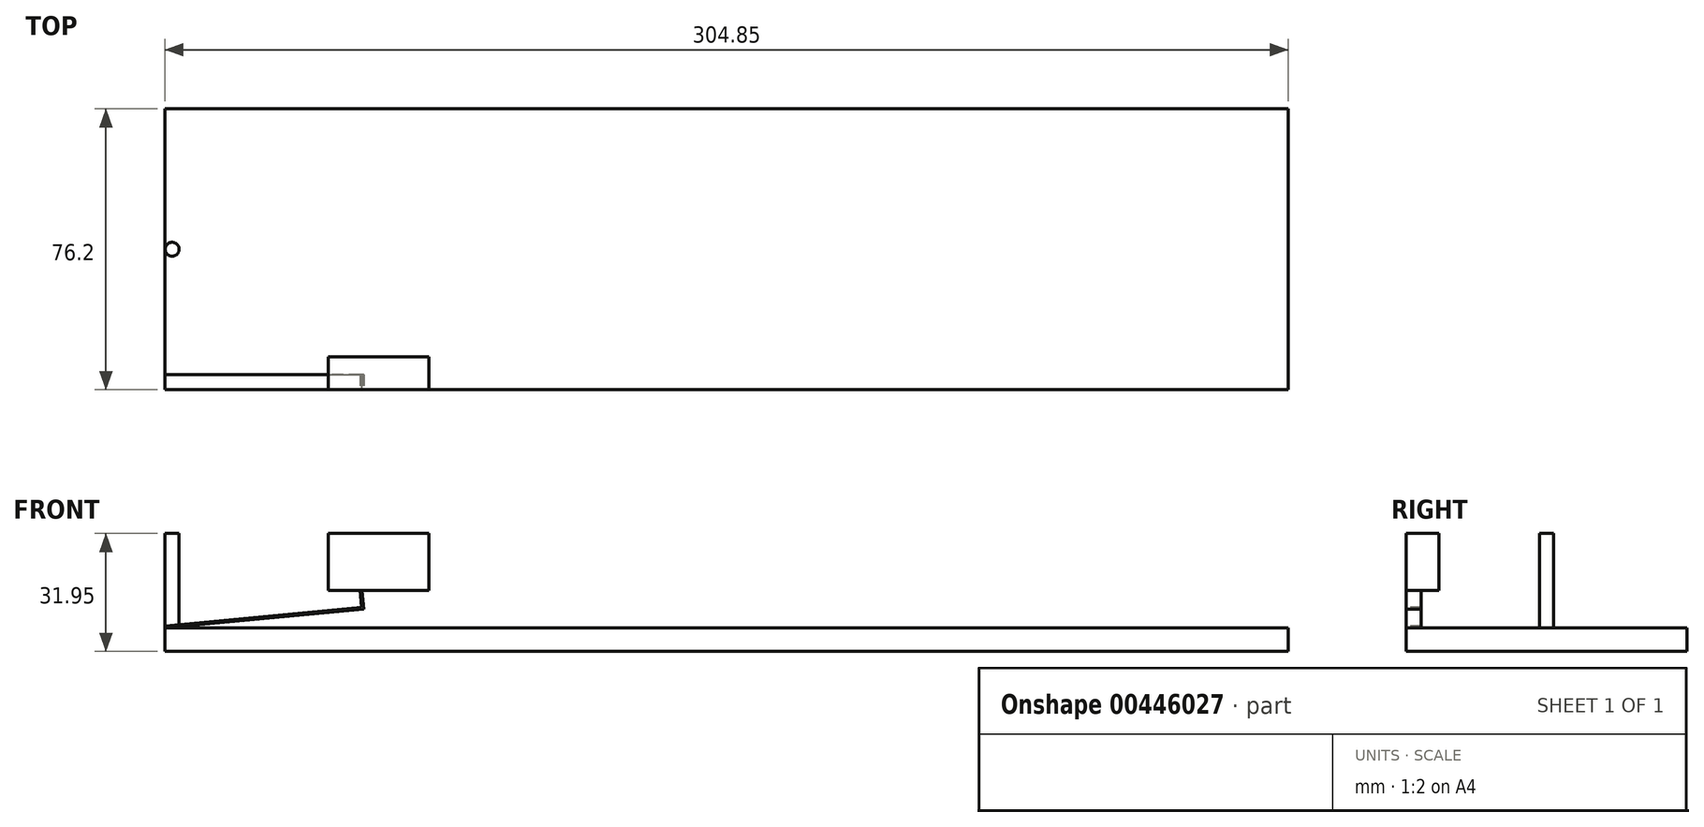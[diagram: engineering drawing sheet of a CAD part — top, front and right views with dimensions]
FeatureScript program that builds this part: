
annotation { "Feature Type Name" : "Feature", "Feature Type Description" : "" }
export const myFeature = defineFeature(function(context is Context, id is Id, definition is map)
    precondition{}
    {
        {
            var Q0;
            Q0=qCreatedBy(makeId("Top.planeOp"),FACE);
            var sketch = newSketch(context, id + "F0", { "sketchPlane" : qUnion([Q0])});
            skLineSegment(sketch, "E0", {"start": v(0, 0) * mm, "end": v(304.8, 0) * mm});
            skLineSegment(sketch, "E1", {"start": v(304.8, 0) * mm, "end": v(304.8, 76.2) * mm});
            skLineSegment(sketch, "E2", {"start": v(304.8, 76.2) * mm, "end": v(0, 76.2) * mm});
            skLineSegment(sketch, "E3", {"start": v(0, 76.2) * mm, "end": v(0, 0) * mm});
            skSolve(sketch);
        }
        {
            var Q0;
            Q0 = qSketchRegion(id + "F0", true);
            extrude(context, id + "F1", {"entities" : qUnion([Q0]), "depth" : 6.35 * mm});
        }
        {
            var Q0;
            Q0=makeQuery(id+"F1.opExtrude","SWEPT_FACE",FACE,{"disambiguationData":[OSD([sQuery(id+"F0.wireOp",EDGE,"E0")])]});
            var sketch = newSketch(context, id + "F2", { "sketchPlane" : qUnion([Q0])});
            skLineSegment(sketch, "E4", {"start": v(0, 6.35) * mm, "end": v(53.86, 11.44) * mm});
            skLineSegment(sketch, "E5", {"start": v(53.86, 11.44) * mm, "end": v(53.81, 11.95) * mm});
            skLineSegment(sketch, "E6", {"start": v(0, 6.35) * mm, "end": v(-0.05, 6.86) * mm});
            skLineSegment(sketch, "E7", {"start": v(-0.05, 6.86) * mm, "end": v(53.81, 11.95) * mm});
            skLineSegment(sketch, "E8", {"start": v(53.86, 11.44) * mm, "end": v(53.38, 16.5) * mm});
            skLineSegment(sketch, "E9", {"start": v(53.38, 16.5) * mm, "end": v(52.88, 16.45) * mm});
            skLineSegment(sketch, "E10", {"start": v(52.88, 16.45) * mm, "end": v(53.35, 11.44) * mm});
            skLineSegment(sketch, "E11", {"start": v(53.35, 11.44) * mm, "end": v(53.86, 11.44) * mm});
            skSolve(sketch);
        }
        {
            var Q0;
            Q0 = qSketchRegion(id + "F2", true);
            extrude(context, id + "F3", {"entities" : qUnion([Q0]), "oppositeDirection" : true, "depth" : 4.06 * mm});
        }
        {
            var Q0;
            Q0=makeQuery(id+"F3.opExtrude","CAP_FACE",FACE,{"disambiguationData":[OSD([sQuery(id+"F2.wireOp",EDGE,"E4"),sQuery(id+"F2.wireOp",EDGE,"E6"),sQuery(id+"F2.wireOp",EDGE,"E7"),sQuery(id+"F2.wireOp",EDGE,"E8"),sQuery(id+"F2.wireOp",EDGE,"E9"),sQuery(id+"F2.wireOp",EDGE,"E10")])],"isStart":false});
            var sketch = newSketch(context, id + "F4", { "sketchPlane" : qUnion([Q0])});
            skLineSegment(sketch, "E12", {"start": v(-52.88, 16.45) * mm, "end": v(-71.64, 16.45) * mm});
            skLineSegment(sketch, "E13", {"start": v(-71.64, 16.45) * mm, "end": v(-71.64, 31.95) * mm});
            skLineSegment(sketch, "E14", {"start": v(-71.64, 31.95) * mm, "end": v(-44.2, 31.95) * mm});
            skLineSegment(sketch, "E15", {"start": v(-44.2, 31.95) * mm, "end": v(-44.2, 16.45) * mm});
            skLineSegment(sketch, "E16", {"start": v(-44.2, 16.45) * mm, "end": v(-53.38, 16.5) * mm});
            skSolve(sketch);
        }
        {
            var Q0;
            {var subQ0=sQuery(id+"F4.wireOp",EDGE,"E13");Q0=makeQuery(id+"F4.imprint","IMPRINT",FACE,{"disambiguationData":[TD([[makeQuery(id+"F4.imprint","IMPRINT",EDGE,{"derivedFrom":subQ0}),-1.0]])]});}
            extrude(context, id + "F5", {"entities" : qUnion([Q0]), "operationType" : NewBodyOperationType.ADD, "oppositeDirection" : true, "depth" : 4.06 * mm});
        }
        {
            var Q0;
            {var subQ0=sQuery(id+"F2.wireOp",EDGE,"E8");Q0=makeQuery(id+"F5.boolean.opBoolean","MERGE",FACE,{"derivedFrom":[makeQuery(id+"F3.opExtrude","CAP_FACE",FACE,{"disambiguationData":[OSD([sQuery(id+"F2.wireOp",EDGE,"E4"),sQuery(id+"F2.wireOp",EDGE,"E6"),sQuery(id+"F2.wireOp",EDGE,"E7"),subQ0,sQuery(id+"F2.wireOp",EDGE,"E9"),sQuery(id+"F2.wireOp",EDGE,"E10")])],"isStart":false}),makeQuery(id+"F5.opExtrude","CAP_FACE",FACE,{"disambiguationData":[OSD([subQ0,sQuery(id+"F4.wireOp",EDGE,"E12"),sQuery(id+"F4.wireOp",EDGE,"E13"),sQuery(id+"F4.wireOp",EDGE,"E14"),sQuery(id+"F4.wireOp",EDGE,"E15"),sQuery(id+"F4.wireOp",EDGE,"E16")])],"isStart":true})]});}
            var sketch = newSketch(context, id + "F6", { "sketchPlane" : qUnion([Q0])});
            skLineSegment(sketch, "E17", {"start": v(-44.2, 16.45) * mm, "end": v(-44.2, 31.95) * mm});
            skLineSegment(sketch, "E18", {"start": v(-44.2, 31.95) * mm, "end": v(-71.64, 31.95) * mm});
            skLineSegment(sketch, "E19", {"start": v(-71.64, 31.95) * mm, "end": v(-71.64, 16.45) * mm});
            skLineSegment(sketch, "E20", {"start": v(-71.64, 16.45) * mm, "end": v(-44.2, 16.45) * mm});
            skSolve(sketch);
        }
        {
            var Q0;
            Q0 = qSketchRegion(id + "F6", true);
            extrude(context, id + "F7", {"entities" : qUnion([Q0]), "operationType" : NewBodyOperationType.ADD, "depth" : 4.83 * mm});
        }
        {
            var Q0;
            Q0=makeQuery(id+"F1.opExtrude","CAP_FACE",FACE,{"disambiguationData":[OSD([sQuery(id+"F0.wireOp",EDGE,"E0"),sQuery(id+"F0.wireOp",EDGE,"E1"),sQuery(id+"F0.wireOp",EDGE,"E2"),sQuery(id+"F0.wireOp",EDGE,"E3")])],"isStart":false});
            var sketch = newSketch(context, id + "F8", { "sketchPlane" : qUnion([Q0])});
            skLineSegment(sketch, "E21", {"start": v(0, 38.1) * mm, "end": v(1.9, 38.1) * mm});
            skPoint(sketch, "E21.endSnap0", {"position": v(0, 38.1) * mm});
            skCircle(sketch, "E22", {"center": v(1.9, 38.1) * mm, "radius": 1.9 * mm});
            skSolve(sketch);
        }
        {
            var Q0;
            Q0=makeQuery(id+"F8.imprint","IMPRINT",FACE,{"disambiguationData":[TD([[makeQuery(id+"F8.imprint","IMPRINT",EDGE,{"derivedFrom":sQuery(id+"F8.wireOp",EDGE,"E22")}),1.0]])]});
            extrude(context, id + "F9", {"entities" : qUnion([Q0]), "operationType" : NewBodyOperationType.ADD, "depth" : 25.6 * mm});
        }
    });
